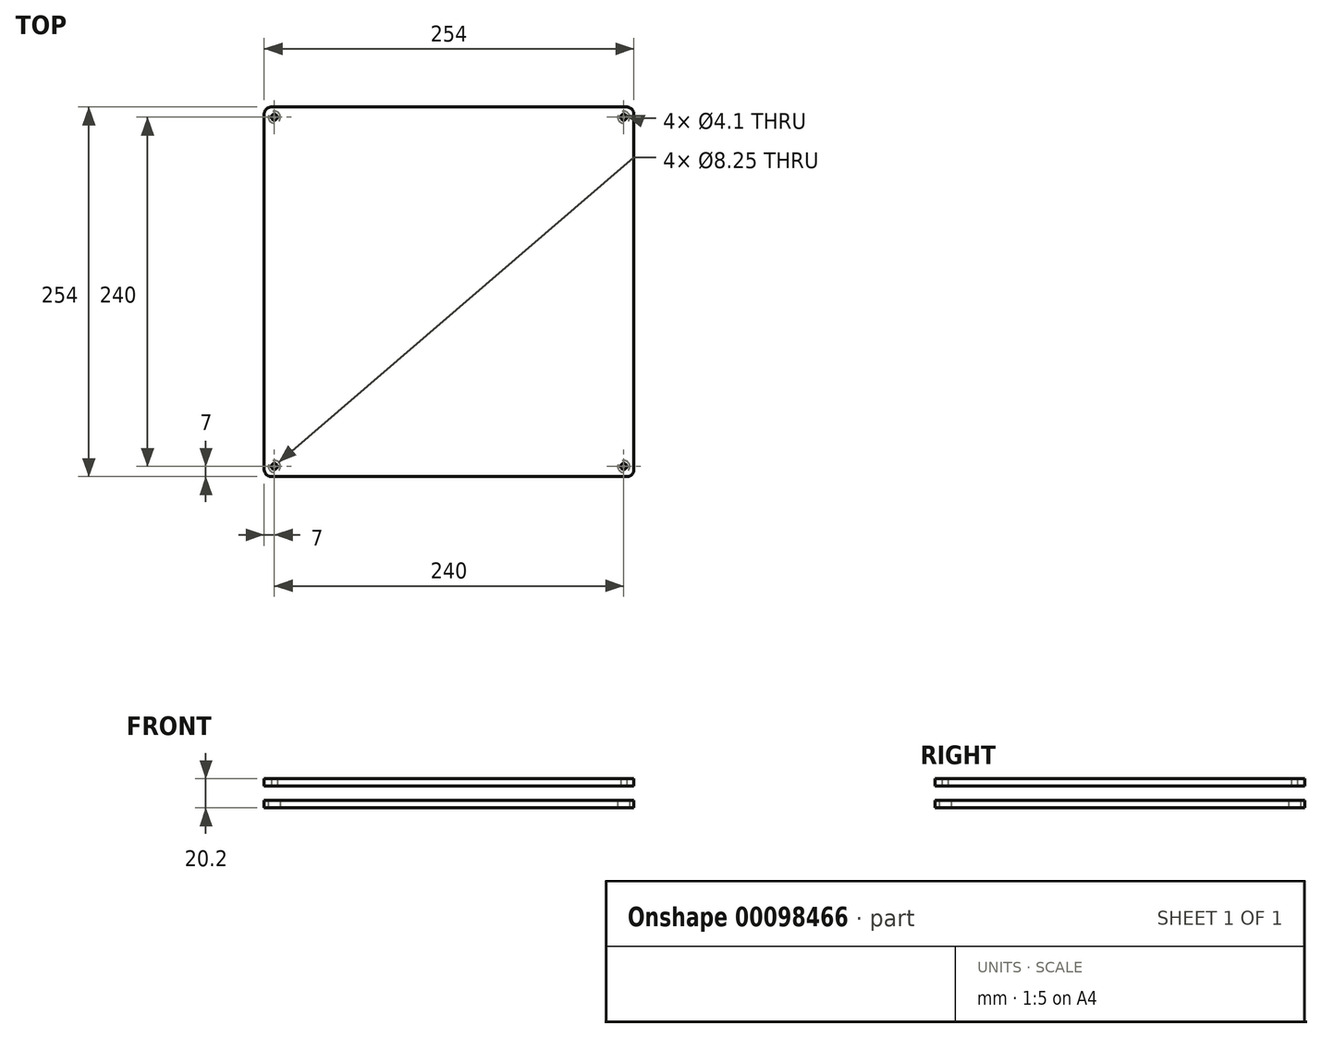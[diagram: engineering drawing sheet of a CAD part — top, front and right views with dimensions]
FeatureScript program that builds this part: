
annotation { "Feature Type Name" : "Feature", "Feature Type Description" : "" }
export const myFeature = defineFeature(function(context is Context, id is Id, definition is map)
    precondition{}
    {
        {
            var Q0;
            Q0=qCreatedBy(makeId("Top.planeOp"),FACE);
            var sketch = newSketch(context, id + "F0", { "sketchPlane" : qUnion([Q0])});
            skLineSegment(sketch, "E0.bottom", {"start": v(127, -127) * mm, "end": v(-127, -127) * mm});
            skLineSegment(sketch, "E0.top", {"start": v(127, 127) * mm, "end": v(-127, 127) * mm});
            skLineSegment(sketch, "E0.left", {"start": v(127, -127) * mm, "end": v(127, 127) * mm});
            skLineSegment(sketch, "E0.right", {"start": v(-127, -127) * mm, "end": v(-127, 127) * mm});
            skPoint(sketch, "E0.middle", {"position": v(0, 0) * mm});
            skLineSegment(sketch, "E1.bottom", {"start": v(120, 120) * mm, "end": v(-120, 120) * mm, "construction": true});
            skLineSegment(sketch, "E1.top", {"start": v(120, -120) * mm, "end": v(-120, -120) * mm, "construction": true});
            skLineSegment(sketch, "E1.left", {"start": v(120, 120) * mm, "end": v(120, -120) * mm, "construction": true});
            skLineSegment(sketch, "E1.right", {"start": v(-120, 120) * mm, "end": v(-120, -120) * mm, "construction": true});
            skCircle(sketch, "E2", {"center": v(-120, 120) * mm, "radius": 4.12 * mm});
            skCircle(sketch, "E3.MirrorC", {"center": v(120, 120) * mm, "radius": 4.12 * mm});
            skCircle(sketch, "E4.MirrorC", {"center": v(-120, -120) * mm, "radius": 4.12 * mm});
            skCircle(sketch, "E5.MirrorC", {"center": v(120, -120) * mm, "radius": 4.12 * mm});
            skSolve(sketch);
        }
        {
            var Q0;
            Q0 = qSketchRegion(id + "F0", true);
            extrude(context, id + "F1", {"entities" : qUnion([Q0]), "depth" : 5.1 * mm});
        }
        {
            var Q0;
            Q0=makeQuery(id+"F1.opExtrude","CAP_FACE",FACE,{"disambiguationData":[OSD([sQuery(id+"F0.wireOp",EDGE,"E0.bottom"),sQuery(id+"F0.wireOp",EDGE,"E0.top"),sQuery(id+"F0.wireOp",EDGE,"E0.left"),sQuery(id+"F0.wireOp",EDGE,"E0.right"),sQuery(id+"F0.wireOp",EDGE,"E2"),sQuery(id+"F0.wireOp",EDGE,"E3.MirrorC"),sQuery(id+"F0.wireOp",EDGE,"E4.MirrorC"),sQuery(id+"F0.wireOp",EDGE,"E5.MirrorC")])],"isStart":false});
            cPlane(context, id + "F2", {"entities" : qUnion([Q0]), "cplaneType" : CPlaneType.OFFSET, "offset" : 10 * mm, "width" : 150 * mm, "height" : 150 * mm});
        }
        {
            var Q0;
            Q0=qCreatedBy(id+"F2.planeOp",FACE);
            var sketch = newSketch(context, id + "F3", { "sketchPlane" : qUnion([Q0])});
            skLineSegment(sketch, "E6.0", {"start": v(127, 127) * mm, "end": v(-127, 127) * mm});
            skLineSegment(sketch, "E6.1", {"start": v(-127, -127) * mm, "end": v(-127, 127) * mm});
            skLineSegment(sketch, "E6.2", {"start": v(127, -127) * mm, "end": v(-127, -127) * mm});
            skLineSegment(sketch, "E6.3", {"start": v(127, -127) * mm, "end": v(127, 127) * mm});
            skCircle(sketch, "E6.4", {"center": v(120, 120) * mm, "radius": 4.12 * mm, "construction": true});
            skCircle(sketch, "E6.5", {"center": v(-120, 120) * mm, "radius": 4.12 * mm, "construction": true});
            skCircle(sketch, "E6.6", {"center": v(-120, -120) * mm, "radius": 4.12 * mm, "construction": true});
            skCircle(sketch, "E6.7", {"center": v(120, -120) * mm, "radius": 4.12 * mm, "construction": true});
            skCircle(sketch, "E7", {"center": v(-120, 120) * mm, "radius": 2.05 * mm});
            skCircle(sketch, "E8.MirrorC", {"center": v(120, 120) * mm, "radius": 2.05 * mm});
            skCircle(sketch, "E9.MirrorC", {"center": v(-120, -120) * mm, "radius": 2.05 * mm});
            skCircle(sketch, "E10.MirrorC", {"center": v(120, -120) * mm, "radius": 2.05 * mm});
            skSolve(sketch);
        }
        {
            var Q0;
            Q0 = qSketchRegion(id + "F3", true);
            extrude(context, id + "F4", {"entities" : qUnion([Q0]), "depth" : 5.1 * mm});
        }
        {
            var Q0;
            Q0=makeQuery(id+"F1.opExtrude","SWEPT_EDGE",EDGE,{"disambiguationData":[OSD([sQuery(id+"F0.wireOp",EDGE,"E0.top"),sQuery(id+"F0.wireOp",EDGE,"E0.right")])]});
            var Q1;
            Q1=makeQuery(id+"F1.opExtrude","SWEPT_EDGE",EDGE,{"disambiguationData":[OSD([sQuery(id+"F0.wireOp",EDGE,"E0.top"),sQuery(id+"F0.wireOp",EDGE,"E0.left")])]});
            var Q2;
            Q2=makeQuery(id+"F1.opExtrude","SWEPT_EDGE",EDGE,{"disambiguationData":[OSD([sQuery(id+"F0.wireOp",EDGE,"E0.bottom"),sQuery(id+"F0.wireOp",EDGE,"E0.left")])]});
            var Q3;
            Q3=makeQuery(id+"F1.opExtrude","SWEPT_EDGE",EDGE,{"disambiguationData":[OSD([sQuery(id+"F0.wireOp",EDGE,"E0.bottom"),sQuery(id+"F0.wireOp",EDGE,"E0.right")])]});
            fillet(context, id + "F5", {"entities" : qUnion([Q0, Q1, Q2, Q3]), "radius" : 5 * mm, "tangentPropagation" : true, "allowEdgeOverflow" : false});
        }
        {
            var Q0;
            Q0=makeQuery(id+"F4.opExtrude","SWEPT_EDGE",EDGE,{"disambiguationData":[OSD([sQuery(id+"F3.wireOp",EDGE,"E6.1"),sQuery(id+"F3.wireOp",EDGE,"E6.2")])]});
            var Q1;
            Q1=makeQuery(id+"F4.opExtrude","SWEPT_EDGE",EDGE,{"disambiguationData":[OSD([sQuery(id+"F3.wireOp",EDGE,"E6.2"),sQuery(id+"F3.wireOp",EDGE,"E6.3")])]});
            var Q2;
            Q2=makeQuery(id+"F4.opExtrude","SWEPT_EDGE",EDGE,{"disambiguationData":[OSD([sQuery(id+"F3.wireOp",EDGE,"E6.0"),sQuery(id+"F3.wireOp",EDGE,"E6.3")])]});
            var Q3;
            Q3=makeQuery(id+"F4.opExtrude","SWEPT_EDGE",EDGE,{"disambiguationData":[OSD([sQuery(id+"F3.wireOp",EDGE,"E6.0"),sQuery(id+"F3.wireOp",EDGE,"E6.1")])]});
            fillet(context, id + "F6", {"entities" : qUnion([Q0, Q1, Q2, Q3]), "radius" : 5 * mm, "tangentPropagation" : true, "allowEdgeOverflow" : false});
        }
    });
